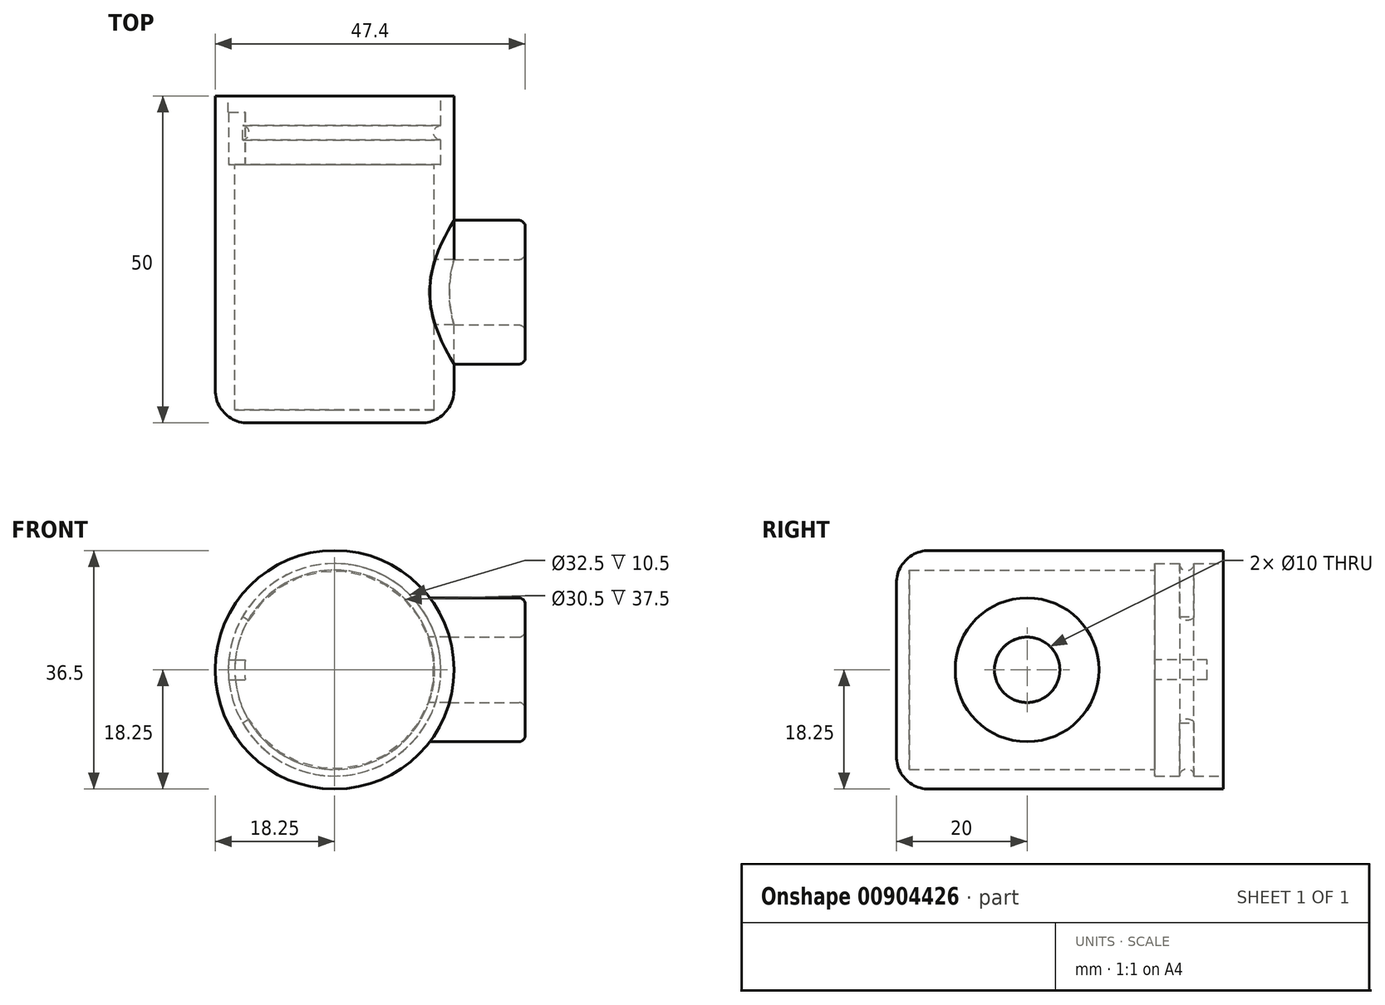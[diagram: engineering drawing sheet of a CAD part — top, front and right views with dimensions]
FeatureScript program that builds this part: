
annotation { "Feature Type Name" : "Feature", "Feature Type Description" : "" }
export const myFeature = defineFeature(function(context is Context, id is Id, definition is map)
    precondition{}
    {
        {
            var Q0;
            Q0=qCreatedBy(makeId("Front.planeOp"),FACE);
            var sketch = newSketch(context, id + "F0", { "sketchPlane" : qUnion([Q0])});
            skCircle(sketch, "E0", {"center": v(0, 0) * mm, "radius": 15.25 * mm});
            skCircle(sketch, "E1.0", {"center": v(0, 0) * mm, "radius": 18.25 * mm});
            skSolve(sketch);
        }
        {
            var Q0;
            Q0 = qSketchRegion(id + "F0", true);
            extrude(context, id + "F1", {"entities" : qUnion([Q0]), "depth" : 50 * mm, "offsetDistance" : 25 * mm});
        }
        {
            var Q0;
            Q0=makeQuery(id+"F1.opExtrude","CAP_FACE",FACE,{"disambiguationData":[OSD([sQuery(id+"F0.wireOp",EDGE,"E0"),sQuery(id+"F0.wireOp",EDGE,"E1.0")])],"isStart":false});
            var sketch = newSketch(context, id + "F2", { "sketchPlane" : qUnion([Q0])});
            skCircle(sketch, "E2.0", {"center": v(0, 0) * mm, "radius": 18.25 * mm});
            skSolve(sketch);
        }
        {
            var Q0;
            Q0 = qSketchRegion(id + "F2", true);
            extrude(context, id + "F3", {"entities" : qUnion([Q0]), "operationType" : NewBodyOperationType.ADD, "oppositeDirection" : true, "depth" : 2 * mm, "offsetDistance" : 25 * mm});
        }
        {
            var Q0;
            Q0=makeQuery(id+"F1.opExtrude","CAP_EDGE",EDGE,{"disambiguationData":[OSD([sQuery(id+"F0.wireOp",EDGE,"E1.0")])],"isStart":false});
            fillet(context, id + "F4", {"entities" : qUnion([Q0]), "radius" : 5 * mm, "tangentPropagation" : true, "allowEdgeOverflow" : false});
        }
        {
            var Q0;
            Q0=makeQuery(id+"F1.opExtrude","CAP_FACE",FACE,{"disambiguationData":[OSD([sQuery(id+"F0.wireOp",EDGE,"E0"),sQuery(id+"F0.wireOp",EDGE,"E1.0")])],"isStart":true});
            var sketch = newSketch(context, id + "F5", { "sketchPlane" : qUnion([Q0])});
            skCircle(sketch, "E3.0", {"center": v(0, 0) * mm, "radius": 16.25 * mm});
            skSolve(sketch);
        }
        {
            var Q0;
            Q0 = qSketchRegion(id + "F5", true);
            extrude(context, id + "F6", {"entities" : qUnion([Q0]), "operationType" : NewBodyOperationType.REMOVE, "oppositeDirection" : true, "depth" : 10.5 * mm, "offsetDistance" : 25 * mm});
        }
        {
            var Q0;
            Q0=qCreatedBy(makeId("Right.planeOp"),FACE);
            var sketch = newSketch(context, id + "F7", { "sketchPlane" : qUnion([Q0])});
            skCircle(sketch, "E4", {"center": v(-30, 0) * mm, "radius": 5 * mm});
            skSolve(sketch);
        }
        {
            var Q0;
            Q0 = qSketchRegion(id + "F7", true);
            extrude(context, id + "F8", {"entities" : qUnion([Q0]), "operationType" : NewBodyOperationType.REMOVE, "endBound" : BoundingType.THROUGH_ALL, "depth" : 25 * mm, "offsetDistance" : 25 * mm});
        }
        {
            var Q0;
            Q0=qCreatedBy(makeId("Right.planeOp"),FACE);
            cPlane(context, id + "F9", {"entities" : qUnion([Q0]), "cplaneType" : CPlaneType.OFFSET, "offset" : (23.15 + 6) * mm, "width" : 150 * mm, "height" : 150 * mm});
        }
        {
            var Q0;
            Q0=qCreatedBy(id+"F9.planeOp",FACE);
            var sketch = newSketch(context, id + "F10", { "sketchPlane" : qUnion([Q0])});
            skCircle(sketch, "E5.0", {"center": v(-30, 0) * mm, "radius": 5 * mm});
            skCircle(sketch, "E6.0", {"center": v(-30, 0) * mm, "radius": 11 * mm});
            skSolve(sketch);
        }
        {
            var Q0;
            Q0 = qSketchRegion(id + "F10", true);
            var Q1;
            Q1=makeQuery(id+"F1.opExtrude","SWEPT_FACE",FACE,{"disambiguationData":[OSD([sQuery(id+"F0.wireOp",EDGE,"E1.0")])]});
            extrude(context, id + "F11", {"entities" : qUnion([Q0]), "endBound" : BoundingType.UP_TO_SURFACE, "oppositeDirection" : true, "depth" : 25 * mm, "endBoundEntityFace" : qUnion([Q1]), "offsetDistance" : 25 * mm});
        }
        {
            var Q0;
            Q0=makeQuery(id+"F11.opExtrude","CAP_EDGE",EDGE,{"disambiguationData":[OSD([sQuery(id+"F10.wireOp",EDGE,"E5.0")])],"isStart":true});
            var Q1;
            Q1=makeQuery(id+"F11.opExtrude","CAP_EDGE",EDGE,{"disambiguationData":[OSD([sQuery(id+"F10.wireOp",EDGE,"E6.0")])],"isStart":true});
            fillet(context, id + "F12", {"entities" : qUnion([Q0, Q1]), "radius" : 1 * mm, "tangentPropagation" : true, "allowEdgeOverflow" : false});
        }
        {
            var Q0;
            Q0=makeQuery(id+"F6.boolean.opBoolean","COPY",FACE,{"derivedFrom":makeQuery(id+"F6.opExtrude","CAP_FACE",FACE,{"disambiguationData":[OSD([sQuery(id+"F5.wireOp",EDGE,"E3.0")])],"isStart":false})});
            var sketch = newSketch(context, id + "F13", { "sketchPlane" : qUnion([Q0])});
            skLineSegment(sketch, "E7", {"start": v(0, 0) * mm, "end": v(38.18, 0) * mm, "construction": true});
            skArc(sketch, "E8.0", {"start": v(16.18, -1.5) * mm, "mid": v(16.25, 0) * mm, "end": v(16.18, 1.5) * mm});
            skArc(sketch, "E9", {"start": v(13.67, -1.5) * mm, "mid": v(13.75, 0) * mm, "end": v(13.67, 1.5) * mm});
            skLineSegment(sketch, "E10", {"start": v(16.18, 1.5) * mm, "end": v(13.67, 1.5) * mm});
            skLineSegment(sketch, "E11.MirrorCS", {"start": v(16.18, -1.5) * mm, "end": v(13.67, -1.5) * mm});
            skSolve(sketch);
        }
        {
            var Q0;
            Q0 = qSketchRegion(id + "F13", true);
            extrude(context, id + "F14", {"entities" : qUnion([Q0]), "operationType" : NewBodyOperationType.ADD, "depth" : 8 * mm, "offsetDistance" : 25 * mm});
        }
        {
            var Q0;
            Q0=qCreatedBy(makeId("Top.planeOp"),FACE);
            var sketch = newSketch(context, id + "F15", { "sketchPlane" : qUnion([Q0])});
            skLineSegment(sketch, "E12", {"start": v(0, 0) * mm, "end": v(0, -26.3) * mm, "construction": true});
            skCircle(sketch, "E13.converted", {"center": v(16.25, -5.6) * mm, "radius": 1.1 * mm});
            skPoint(sketch, "E14.orphan", {"position": v(16.25, -4.5) * mm});
            skSolve(sketch);
        }
        {
            var Q0;
            Q0 = qSketchRegion(id + "F15", true);
            var Q1;
            Q1=sQuery(id+"F15.wireOp",EDGE,"E12");
            revolve(context, id + "F16", {"operationType" : NewBodyOperationType.ADD, "surfaceOperationType" : NewSurfaceOperationType.NEW, "entities" : qUnion([Q0]), "axis" : qUnion([Q1]), "revolveType" : RevolveType.SYMMETRIC, "angle" : 300 * degree});
        }
    });
